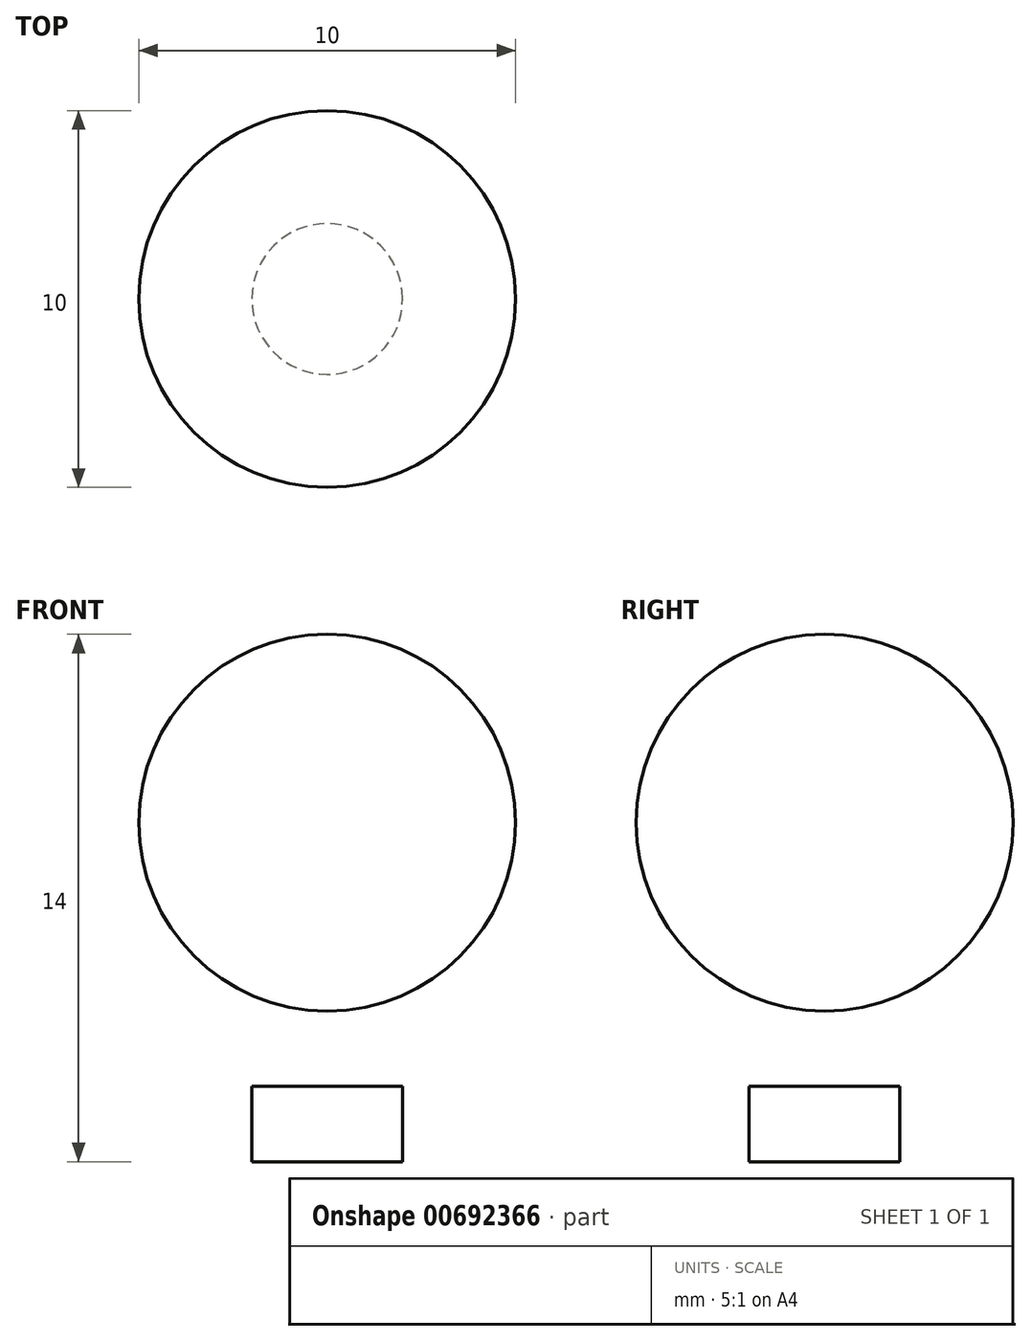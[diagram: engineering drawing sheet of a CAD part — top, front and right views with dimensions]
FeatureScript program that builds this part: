
annotation { "Feature Type Name" : "Feature", "Feature Type Description" : "" }
export const myFeature = defineFeature(function(context is Context, id is Id, definition is map)
    precondition{}
    {
        {
            var Q0;
            Q0=qCreatedBy(makeId("Front.planeOp"),FACE);
            var sketch = newSketch(context, id + "F0", { "sketchPlane" : qUnion([Q0])});
            skLineSegment(sketch, "E0.bottom", {"start": v(0, 0) * mm, "end": v(-5, 0) * mm});
            skLineSegment(sketch, "E0.top", {"start": v(0, 5) * mm, "end": v(-5, 5) * mm});
            skLineSegment(sketch, "E0.left", {"start": v(0, 0) * mm, "end": v(0, 5) * mm});
            skLineSegment(sketch, "E0.right", {"start": v(-5, 0) * mm, "end": v(-5, 5) * mm});
            skLineSegment(sketch, "E1", {"start": v(0, 5) * mm, "end": v(0, 14) * mm});
            skLineSegment(sketch, "E2", {"start": v(0, 5) * mm, "end": v(0, 9) * mm});
            skArc(sketch, "E3", {"start": v(0, 14) * mm, "mid": v(-5, 9) * mm, "end": v(0, 4) * mm});
            skLineSegment(sketch, "E4.bottom", {"start": v(0, 0) * mm, "end": v(-2, 0) * mm});
            skLineSegment(sketch, "E4.top", {"start": v(0, 2) * mm, "end": v(-2, 2) * mm});
            skLineSegment(sketch, "E4.left", {"start": v(0, 0) * mm, "end": v(0, 2) * mm});
            skLineSegment(sketch, "E4.right", {"start": v(-2, 0) * mm, "end": v(-2, 2) * mm});
            skSolve(sketch);
        }
        {
            var Q0;
            {var subQ4=sQuery(id+"F0.wireOp",EDGE,"E1");Q0=makeQuery(id+"F0.imprint","IMPRINT",FACE,{"disambiguationData":[TD([[makeQuery(id+"F0.imprint","IMPRINT",EDGE,{"derivedFrom":subQ4}),1.0]])]});}
            var Q1;
            {var subQ0=sQuery(id+"F0.wireOp",EDGE,"E0.left");var subQ3=sQuery(id+"F0.wireOp",EDGE,"E3");var subQ5=makeQuery(id+"F0.imprint","INTERSECT",VERTEX,{"derivedFrom":[subQ0,subQ3]});Q1=makeQuery(id+"F0.imprint","IMPRINT",FACE,{"disambiguationData":[TD([[makeQuery(id+"F0.imprint","IMPRINT",EDGE,{"disambiguationData":[TD([[subQ5,1.0]])],"derivedFrom":subQ3}),1.0]])]});}
            var Q2;
            {var subQ1=sQuery(id+"F0.wireOp",EDGE,"E0.bottom");Q2=makeQuery(id+"F0.imprint","IMPRINT",FACE,{"disambiguationData":[TD([[makeQuery(id+"F0.imprint","IMPRINT",EDGE,{"derivedFrom":subQ1}),-1.0]])]});}
            var Q3;
            Q3=sQuery(id+"F0.wireOp",EDGE,"E2");
            revolve(context, id + "F1", {"entities" : qUnion([Q0, Q1, Q2]), "axis" : qUnion([Q3]), "revolveType" : RevolveType.FULL});
        }
    });
